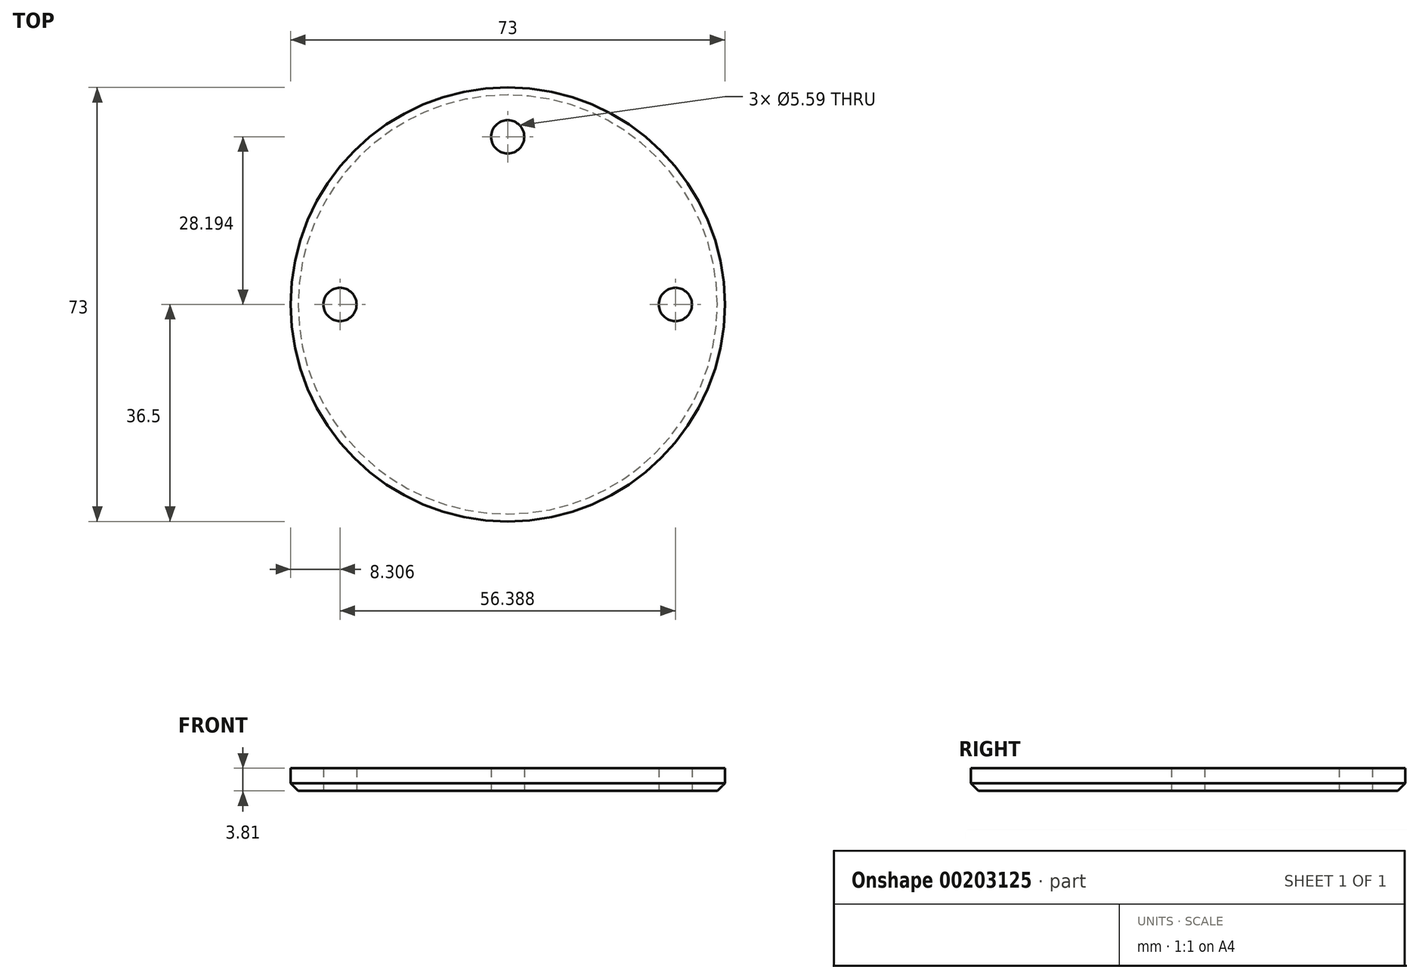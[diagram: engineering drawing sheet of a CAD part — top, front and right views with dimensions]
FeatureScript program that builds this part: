
annotation { "Feature Type Name" : "Feature", "Feature Type Description" : "" }
export const myFeature = defineFeature(function(context is Context, id is Id, definition is map)
    precondition{}
    {
        {
            var Q0;
            Q0=qCreatedBy(makeId("Top.planeOp"),FACE);
            var sketch = newSketch(context, id + "F0", { "sketchPlane" : qUnion([Q0])});
            skCircle(sketch, "E0", {"center": v(0, 0) * mm, "radius": 36.5 * mm});
            skCircle(sketch, "E1", {"center": v(0, 0) * mm, "radius": 28.2 * mm, "construction": true});
            skCircle(sketch, "E2", {"center": v(-28.2, 0) * mm, "radius": 2.8 * mm});
            skCircle(sketch, "E3", {"center": v(0, 28.2) * mm, "radius": 2.8 * mm});
            skCircle(sketch, "E4", {"center": v(28.2, 0) * mm, "radius": 2.8 * mm});
            skSolve(sketch);
        }
        {
            var Q0;
            Q0=makeQuery(id+"F0.imprint","IMPRINT",FACE,{"disambiguationData":[TD([[makeQuery(id+"F0.imprint","IMPRINT",EDGE,{"derivedFrom":sQuery(id+"F0.wireOp",EDGE,"E0")}),1.0]])]});
            extrude(context, id + "F1", {"entities" : qUnion([Q0]), "depth" : 3.8 * mm});
        }
        {
            var Q0;
            Q0=makeQuery(id+"F1.opExtrude","CAP_EDGE",EDGE,{"disambiguationData":[OSD([sQuery(id+"F0.wireOp",EDGE,"E0")])],"isStart":true});
            chamfer(context, id + "F2", {"entities" : qUnion([Q0]), "width" : 1.27 * mm, "tangentPropagation" : true});
        }
    });
